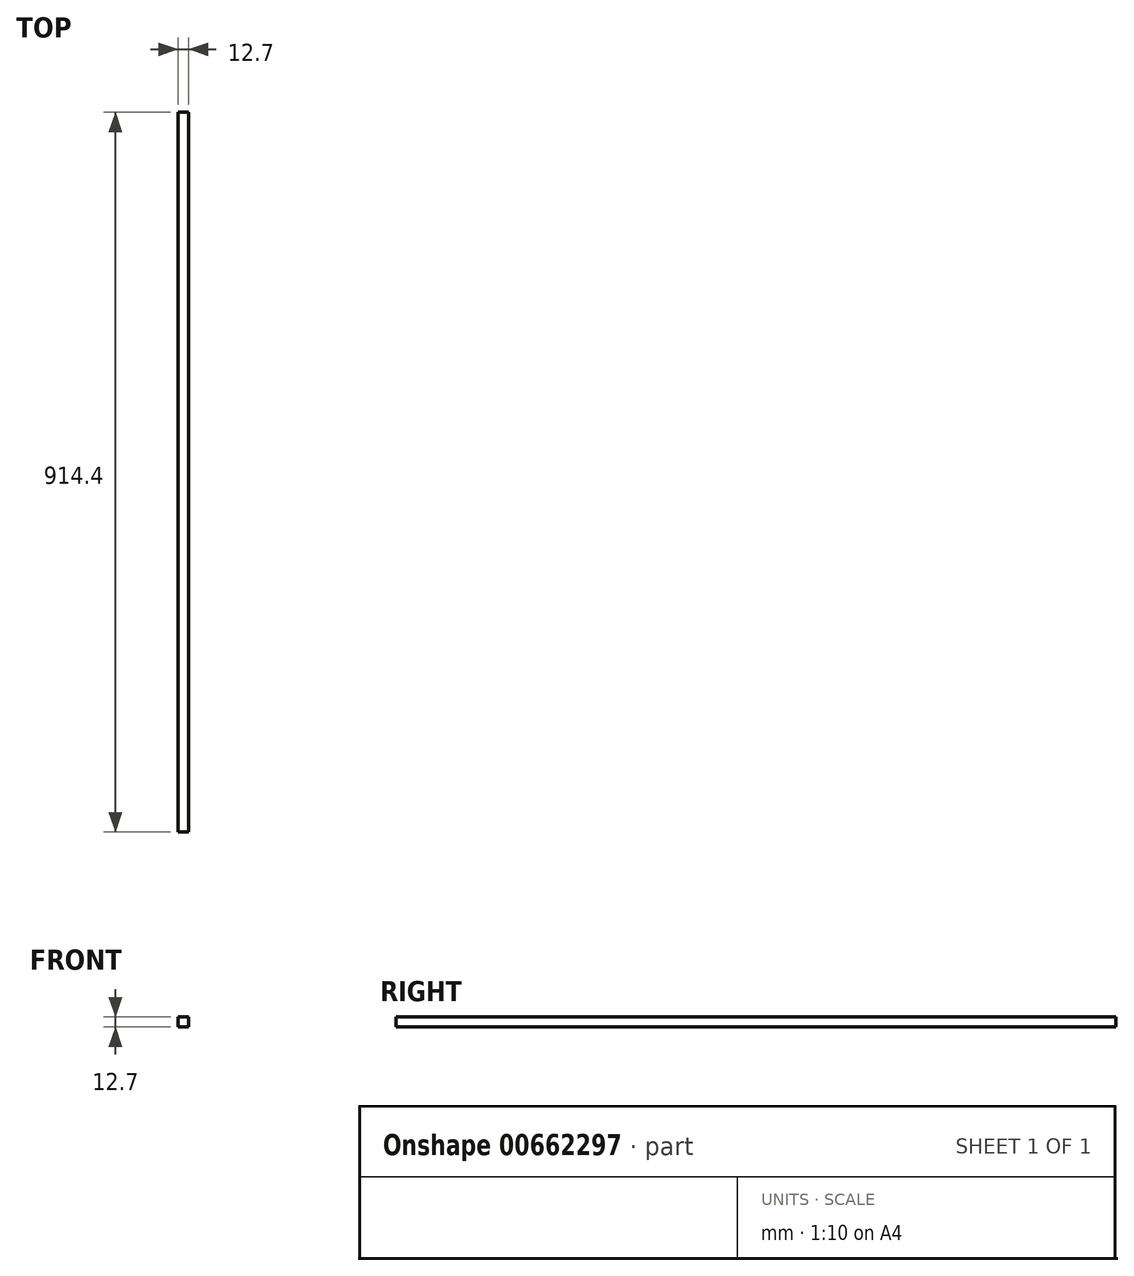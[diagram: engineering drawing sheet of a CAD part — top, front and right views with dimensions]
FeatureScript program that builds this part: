
annotation { "Feature Type Name" : "Feature", "Feature Type Description" : "" }
export const myFeature = defineFeature(function(context is Context, id is Id, definition is map)
    precondition{}
    {
        {
            var Q0;
            Q0=qCreatedBy(makeId("Front.planeOp"),FACE);
            var sketch = newSketch(context, id + "F0", { "sketchPlane" : qUnion([Q0])});
            skLineSegment(sketch, "E0.bottom", {"start": v(8.7, 9.2) * mm, "end": v(-4, 9.2) * mm});
            skLineSegment(sketch, "E0.top", {"start": v(8.7, -3.5) * mm, "end": v(-4, -3.5) * mm});
            skLineSegment(sketch, "E0.left", {"start": v(8.7, 9.2) * mm, "end": v(8.7, -3.5) * mm});
            skLineSegment(sketch, "E0.right", {"start": v(-4, 9.2) * mm, "end": v(-4, -3.5) * mm});
            skSolve(sketch);
        }
        {
            var Q0;
            Q0 = qSketchRegion(id + "F0", true);
            extrude(context, id + "F1", {"entities" : qUnion([Q0]), "depth" : 914.4 * mm, "offsetDistance" : 25.4 * mm});
        }
    });
